# Revit family: ITK_Панель для 4-ех оптических адаптеров (SC-Duplex в 19 кросс)
name_source: partatom
category: Обобщенные модели
units: mm (PartAtom-declared; Revit-internal decimal feet)

## family parameters
Всегда вертикально = Да
Может служить основой для арматурных стержней = Нет
На основе рабочей плоскости = Нет
Общий = Нет
При загрузке вырезать с полостями = Нет
Размер круглого соединителя = Использовать диаметр
Тип детали = Нормальный
Точка расчета площади = Нет

## types (1)
- FOBX-P8-SCDX
    ADSK_URL страницы изделия = https://www.itk-group.ru
    ADSK_Версия Revit = 2019
    ADSK_Версия семейства = 1.0
    ADSK_Группирование = I. ЩИТЫ И ПУЛЬТЫ
    ADSK_Единица измерения = шт
    ADSK_Завод-изготовитель = IEK
    ADSK_Код изделия = FOBX-P8-SCDX
    ADSK_Масса = 0.1
    ADSK_Материал наименование = Листовая сталь
    ADSK_Наименование = ITK Панель для 4-ех оптических адаптеров (SC-Duplex в 19" кросс)
    IEK_URL = https://www.itk-group.ru
    IEK_Описание = Изготовлены из высококачественных материалов.
Соответствие международным стандартам и ГОСТ Р.
    IEK_Цена за единицу = 13.28
    KSI_CMa_Строительные материалы = 10.03.02.06
    KSI_CPr_Строительные изделия = 61.1.04.08
    URL = https://www.iek.ru
    Высота = 32 мм
    Глубина = 2 мм
    Изготовитель = ITK
    Материал = Окраска - RAL 7035
    Ширина = 125 мм
